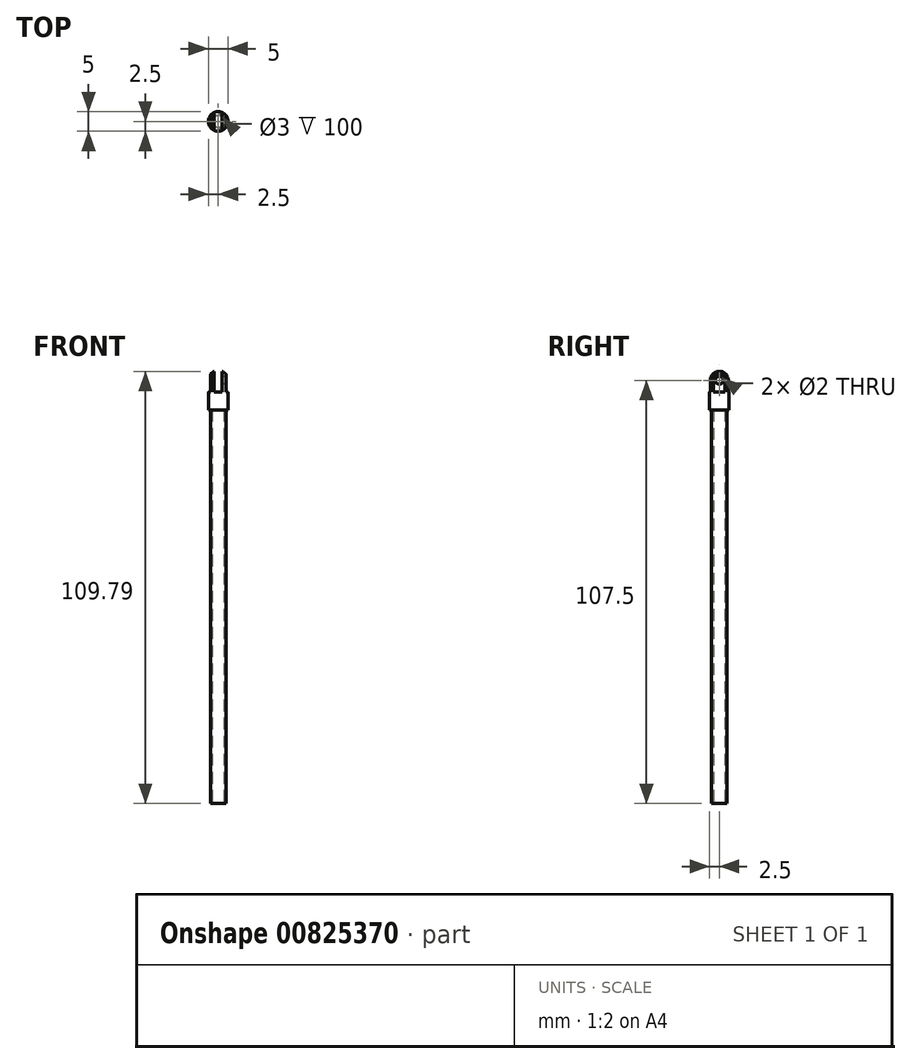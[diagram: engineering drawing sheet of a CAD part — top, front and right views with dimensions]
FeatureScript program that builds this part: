
annotation { "Feature Type Name" : "Feature", "Feature Type Description" : "" }
export const myFeature = defineFeature(function(context is Context, id is Id, definition is map)
    precondition{}
    {
        {
            var Q0;
            Q0=qCreatedBy(makeId("Top.planeOp"),FACE);
            var sketch = newSketch(context, id + "F0", { "sketchPlane" : qUnion([Q0])});
            skCircle(sketch, "E0", {"center": v(0, 0) * mm, "radius": 2 * mm});
            skSolve(sketch);
        }
        {
            var Q0;
            Q0 = qSketchRegion(id + "F0", true);
            extrude(context, id + "F1", {"entities" : qUnion([Q0]), "oppositeDirection" : true, "depth" : 100 * mm, "offsetDistance" : 25 * mm});
        }
        {
            var Q0;
            Q0=makeQuery(id+"F1.opExtrude","CAP_FACE",FACE,{"disambiguationData":[OSD([sQuery(id+"F0.wireOp",EDGE,"E0")])],"isStart":true});
            var sketch = newSketch(context, id + "F2", { "sketchPlane" : qUnion([Q0])});
            skCircle(sketch, "E1", {"center": v(0, 0) * mm, "radius": 2.5 * mm});
            skSolve(sketch);
        }
        {
            var Q0;
            Q0 = qSketchRegion(id + "F2", true);
            extrude(context, id + "F3", {"entities" : qUnion([Q0]), "operationType" : NewBodyOperationType.ADD, "depth" : 10 * mm, "offsetDistance" : 25 * mm});
        }
        {
            var Q0;
            Q0=makeQuery(id+"F3.opExtrude","CAP_EDGE",EDGE,{"disambiguationData":[OSD([sQuery(id+"F2.wireOp",EDGE,"E1")])],"isStart":false});
            fillet(context, id + "F4", {"entities" : qUnion([Q0]), "radius" : 2.5 * mm, "tangentPropagation" : true, "allowEdgeOverflow" : false});
        }
        {
            var Q0;
            Q0=qCreatedBy(makeId("Front.planeOp"),FACE);
            var sketch = newSketch(context, id + "F5", { "sketchPlane" : qUnion([Q0])});
            skLineSegment(sketch, "E2", {"start": v(0, 0) * mm, "end": v(0, 4.5) * mm, "construction": true});
            skLineSegment(sketch, "E3", {"start": v(0, 4.5) * mm, "end": v(1, 4.5) * mm});
            skLineSegment(sketch, "E4", {"start": v(0, 4.5) * mm, "end": v(-1, 4.5) * mm});
            skLineSegment(sketch, "E5", {"start": v(1, 4.5) * mm, "end": v(1, 10.56) * mm});
            skLineSegment(sketch, "E6", {"start": v(-1, 4.5) * mm, "end": v(-1, 10.56) * mm});
            skLineSegment(sketch, "E7", {"start": v(-1, 10.56) * mm, "end": v(1, 10.56) * mm});
            skLineSegment(sketch, "E8", {"start": v(1, 4.5) * mm, "end": v(2, 4.5) * mm, "construction": true});
            skLineSegment(sketch, "E9", {"start": v(-1, 4.5) * mm, "end": v(-2, 4.5) * mm, "construction": true});
            skLineSegment(sketch, "E10.bottom", {"start": v(2, 4.5) * mm, "end": v(3.34, 4.5) * mm});
            skLineSegment(sketch, "E10.top", {"start": v(2, 10.53) * mm, "end": v(3.34, 10.53) * mm});
            skLineSegment(sketch, "E10.left", {"start": v(2, 4.5) * mm, "end": v(2, 10.53) * mm});
            skLineSegment(sketch, "E10.right", {"start": v(3.34, 4.5) * mm, "end": v(3.34, 10.53) * mm});
            skLineSegment(sketch, "E11.bottom", {"start": v(-2, 4.5) * mm, "end": v(-2.99, 4.5) * mm});
            skLineSegment(sketch, "E11.top", {"start": v(-2, 10.56) * mm, "end": v(-2.99, 10.56) * mm});
            skLineSegment(sketch, "E11.left", {"start": v(-2, 4.5) * mm, "end": v(-2, 10.56) * mm});
            skLineSegment(sketch, "E11.right", {"start": v(-2.99, 4.5) * mm, "end": v(-2.99, 10.56) * mm});
            skSolve(sketch);
        }
        {
            var Q0;
            Q0 = qSketchRegion(id + "F5", true);
            extrude(context, id + "F6", {"entities" : qUnion([Q0]), "operationType" : NewBodyOperationType.REMOVE, "endBound" : BoundingType.SYMMETRIC, "oppositeDirection" : true, "depth" : 25 * mm, "offsetDistance" : 25 * mm});
        }
        {
            var Q0;
            Q0=makeQuery(id+"F6.boolean.opBoolean","COPY",FACE,{"derivedFrom":makeQuery(id+"F6.opExtrude","SWEPT_FACE",FACE,{"disambiguationData":[OSD([sQuery(id+"F5.wireOp",EDGE,"E11.left")])]})});
            var sketch = newSketch(context, id + "F7", { "sketchPlane" : qUnion([Q0])});
            skCircle(sketch, "E12", {"center": v(0, 7.5) * mm, "radius": 1 * mm});
            skSolve(sketch);
        }
        {
            var Q0;
            Q0 = qSketchRegion(id + "F7", true);
            extrude(context, id + "F8", {"entities" : qUnion([Q0]), "operationType" : NewBodyOperationType.REMOVE, "oppositeDirection" : true, "depth" : 25 * mm, "offsetDistance" : 25 * mm});
        }
        {
            var Q0;
            Q0=makeQuery(id+"F1.opExtrude","CAP_FACE",FACE,{"disambiguationData":[OSD([sQuery(id+"F0.wireOp",EDGE,"E0")])],"isStart":false});
            var sketch = newSketch(context, id + "F9", { "sketchPlane" : qUnion([Q0])});
            skCircle(sketch, "E13", {"center": v(0, 0) * mm, "radius": 1.5 * mm});
            skSolve(sketch);
        }
        {
            var Q0;
            Q0 = qSketchRegion(id + "F9", true);
            extrude(context, id + "F10", {"entities" : qUnion([Q0]), "operationType" : NewBodyOperationType.REMOVE, "oppositeDirection" : true, "depth" : 100 * mm, "offsetDistance" : 25 * mm});
        }
    });
